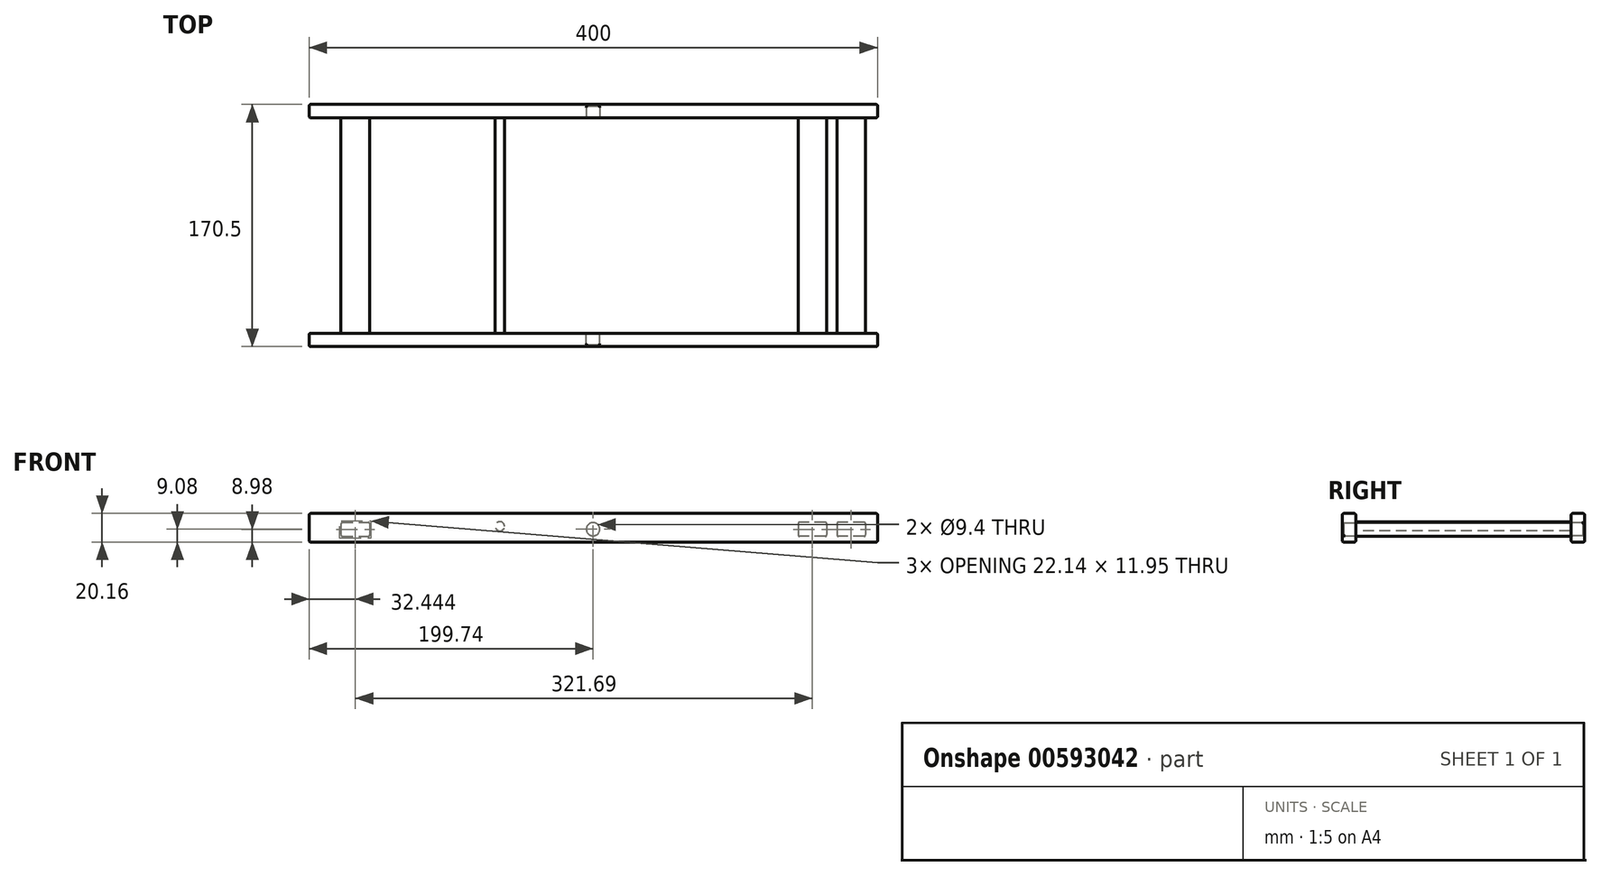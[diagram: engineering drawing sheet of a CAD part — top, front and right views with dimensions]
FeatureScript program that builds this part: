
annotation { "Feature Type Name" : "Feature", "Feature Type Description" : "" }
export const myFeature = defineFeature(function(context is Context, id is Id, definition is map)
    precondition{}
    {
        {
            var Q0;
            Q0=qCreatedBy(makeId("Front.planeOp"),FACE);
            var sketch = newSketch(context, id + "F0", { "sketchPlane" : qUnion([Q0])});
            skLineSegment(sketch, "E0.bottom", {"start": v(200, -10.07) * mm, "end": v(-200, -10.08) * mm});
            skLineSegment(sketch, "E0.top", {"start": v(200, 10.08) * mm, "end": v(-200, 10.07) * mm});
            skLineSegment(sketch, "E0.left", {"start": v(200, -10.07) * mm, "end": v(200, 10.08) * mm});
            skLineSegment(sketch, "E0.right", {"start": v(-200, -10.08) * mm, "end": v(-200, 10.07) * mm});
            skPoint(sketch, "E0.middle", {"position": v(0, 0) * mm});
            skSolve(sketch);
        }
        {
            var Q0;
            Q0=makeQuery(id+"F0.imprint","IMPRINT",FACE,{"disambiguationData":[TD([[makeQuery(id+"F0.imprint","IMPRINT",EDGE,{"derivedFrom":sQuery(id+"F0.wireOp",EDGE,"E0.bottom")}),-1.0]])]});
            extrude(context, id + "F1", {"entities" : qUnion([Q0]), "depth" : 9.4 * mm});
        }
        {
            var Q0;
            Q0=makeQuery(id+"F1.opExtrude","CAP_FACE",FACE,{"disambiguationData":[OSD([sQuery(id+"F0.wireOp",EDGE,"E0.bottom"),sQuery(id+"F0.wireOp",EDGE,"E0.top"),sQuery(id+"F0.wireOp",EDGE,"E0.left"),sQuery(id+"F0.wireOp",EDGE,"E0.right")])],"isStart":false});
            var sketch = newSketch(context, id + "F2", { "sketchPlane" : qUnion([Q0])});
            skLineSegment(sketch, "E1.bottom", {"start": v(-177.62, 3.87) * mm, "end": v(-157.49, 3.87) * mm});
            skLineSegment(sketch, "E1.top", {"start": v(-177.62, -6.08) * mm, "end": v(-157.49, -6.08) * mm});
            skLineSegment(sketch, "E1.left", {"start": v(-177.62, 3.87) * mm, "end": v(-177.62, -6.08) * mm});
            skLineSegment(sketch, "E1.right", {"start": v(-157.49, 3.87) * mm, "end": v(-157.49, -6.07) * mm});
            skLineSegment(sketch, "E2.bottom", {"start": v(191.5, 3.88) * mm, "end": v(171.36, 3.88) * mm});
            skLineSegment(sketch, "E2.top", {"start": v(191.5, -6.07) * mm, "end": v(171.36, -6.07) * mm});
            skLineSegment(sketch, "E2.left", {"start": v(191.5, 3.88) * mm, "end": v(191.5, -6.07) * mm});
            skLineSegment(sketch, "E2.right", {"start": v(171.36, 3.88) * mm, "end": v(171.36, -6.07) * mm});
            skLineSegment(sketch, "E3.bottom", {"start": v(164.2, 3.88) * mm, "end": v(144.06, 3.88) * mm});
            skLineSegment(sketch, "E3.top", {"start": v(164.2, -6.07) * mm, "end": v(144.06, -6.07) * mm});
            skLineSegment(sketch, "E3.left", {"start": v(164.2, 3.88) * mm, "end": v(164.2, -6.07) * mm});
            skLineSegment(sketch, "E3.right", {"start": v(144.06, 3.88) * mm, "end": v(144.06, -6.07) * mm});
            skSolve(sketch);
        }
        {
            var Q0;
            Q0=makeQuery(id+"F2.imprint","IMPRINT",FACE,{"disambiguationData":[TD([[makeQuery(id+"F2.imprint","IMPRINT",EDGE,{"derivedFrom":sQuery(id+"F2.wireOp",EDGE,"E1.bottom")}),-1.0]])]});
            var Q1;
            Q1=makeQuery(id+"F2.imprint","IMPRINT",FACE,{"disambiguationData":[TD([[makeQuery(id+"F2.imprint","IMPRINT",EDGE,{"derivedFrom":sQuery(id+"F2.wireOp",EDGE,"E3.bottom")}),1.0]])]});
            var Q2;
            Q2=makeQuery(id+"F2.imprint","IMPRINT",FACE,{"disambiguationData":[TD([[makeQuery(id+"F2.imprint","IMPRINT",EDGE,{"derivedFrom":sQuery(id+"F2.wireOp",EDGE,"E2.bottom")}),1.0]])]});
            extrude(context, id + "F3", {"entities" : qUnion([Q0, Q1, Q2]), "operationType" : NewBodyOperationType.ADD, "depth" : 151.7 * mm});
        }
        {
            var Q0;
            Q0=makeQuery(id+"F3.opExtrude","CAP_FACE",FACE,{"disambiguationData":[OSD([sQuery(id+"F2.wireOp",EDGE,"E1.bottom"),sQuery(id+"F2.wireOp",EDGE,"E1.top"),sQuery(id+"F2.wireOp",EDGE,"E1.left"),sQuery(id+"F2.wireOp",EDGE,"E1.right")])],"isStart":false});
            var sketch = newSketch(context, id + "F4", { "sketchPlane" : qUnion([Q0])});
            skLineSegment(sketch, "E4.bottom", {"start": v(200, -10.07) * mm, "end": v(-200, -10.08) * mm});
            skLineSegment(sketch, "E4.top", {"start": v(200, 10.08) * mm, "end": v(-200, 10.08) * mm});
            skLineSegment(sketch, "E4.left", {"start": v(200, -10.07) * mm, "end": v(200, 10.08) * mm});
            skLineSegment(sketch, "E4.right", {"start": v(-200, -10.08) * mm, "end": v(-200, 10.08) * mm});
            skPoint(sketch, "E4.middle", {"position": v(0, 0) * mm});
            skSolve(sketch);
        }
        {
            var Q0;
            Q0=qSketchRegion(id+"F4",true);
            extrude(context, id + "F5", {"entities" : qUnion([Q0]), "operationType" : NewBodyOperationType.ADD, "depth" : 9.4 * mm});
        }
        {
            var Q0;
            Q0=makeQuery(id+"F5.opExtrude","CAP_FACE",FACE,{"disambiguationData":[OSD([sQuery(id+"F4.wireOp",EDGE,"E4.bottom"),sQuery(id+"F4.wireOp",EDGE,"E4.top"),sQuery(id+"F4.wireOp",EDGE,"E4.left"),sQuery(id+"F4.wireOp",EDGE,"E4.right")])],"isStart":true});
            var sketch = newSketch(context, id + "F6", { "sketchPlane" : qUnion([Q0])});
            skCircle(sketch, "E5", {"center": v(0.26, -1) * mm, "radius": 4.7 * mm});
            skLineSegment(sketch, "E6", {"start": v(200, 0) * mm, "end": v(-200, 0) * mm, "construction": true});
            skSolve(sketch);
        }
        {
            var Q0;
            Q0=makeQuery(id+"F6.imprint","IMPRINT",FACE,{"disambiguationData":[TD([[makeQuery(id+"F6.imprint","IMPRINT",EDGE,{"derivedFrom":sQuery(id+"F6.wireOp",EDGE,"E5")}),1.0]])]});
            extrude(context, id + "F7", {"entities" : qUnion([Q0]), "operationType" : NewBodyOperationType.REMOVE, "oppositeDirection" : true, "depth" : 8.4 * mm});
        }
        {
            var Q0;
            Q0=makeQuery(id+"F1.opExtrude","CAP_FACE",FACE,{"disambiguationData":[OSD([sQuery(id+"F0.wireOp",EDGE,"E0.bottom"),sQuery(id+"F0.wireOp",EDGE,"E0.top"),sQuery(id+"F0.wireOp",EDGE,"E0.left"),sQuery(id+"F0.wireOp",EDGE,"E0.right")])],"isStart":false});
            var sketch = newSketch(context, id + "F8", { "sketchPlane" : qUnion([Q0])});
            skLineSegment(sketch, "E7", {"start": v(-200, 0) * mm, "end": v(200, 0) * mm, "construction": true});
            skCircle(sketch, "E8", {"center": v(-0.26, -1) * mm, "radius": 4.7 * mm});
            skSolve(sketch);
        }
        {
            var Q0;
            Q0=makeQuery(id+"F8.imprint","IMPRINT",FACE,{"disambiguationData":[TD([[makeQuery(id+"F8.imprint","IMPRINT",EDGE,{"derivedFrom":sQuery(id+"F8.wireOp",EDGE,"E8")}),1.0]])]});
            extrude(context, id + "F9", {"entities" : qUnion([Q0]), "operationType" : NewBodyOperationType.REMOVE, "oppositeDirection" : true, "depth" : 8.4 * mm});
        }
        {
            var Q0;
            Q0=makeQuery(id+"F5.opExtrude","CAP_FACE",FACE,{"disambiguationData":[OSD([sQuery(id+"F4.wireOp",EDGE,"E4.bottom"),sQuery(id+"F4.wireOp",EDGE,"E4.top"),sQuery(id+"F4.wireOp",EDGE,"E4.left"),sQuery(id+"F4.wireOp",EDGE,"E4.right")])],"isStart":true});
            var sketch = newSketch(context, id + "F10", { "sketchPlane" : qUnion([Q0])});
            skCircle(sketch, "E9", {"center": v(65.84, 1.08) * mm, "radius": 3.25 * mm});
            skSolve(sketch);
        }
        {
            var Q0;
            Q0=makeQuery(id+"F10.imprint","IMPRINT",FACE,{"disambiguationData":[TD([[makeQuery(id+"F10.imprint","IMPRINT",EDGE,{"derivedFrom":sQuery(id+"F10.wireOp",EDGE,"E9")}),1.0]])]});
            var Q1;
            Q1=makeQuery(id+"F1.opExtrude","CAP_FACE",FACE,{"disambiguationData":[OSD([sQuery(id+"F0.wireOp",EDGE,"E0.bottom"),sQuery(id+"F0.wireOp",EDGE,"E0.top"),sQuery(id+"F0.wireOp",EDGE,"E0.left"),sQuery(id+"F0.wireOp",EDGE,"E0.right")])],"isStart":false});
            extrude(context, id + "F11", {"entities" : qUnion([Q0]), "operationType" : NewBodyOperationType.ADD, "endBound" : BoundingType.UP_TO_SURFACE, "endBoundEntityFace" : qUnion([Q1]), "depth" : 25 * mm});
        }
        {
            var Q0;
            Q0=makeQuery(id+"F5.opExtrude","CAP_FACE",FACE,{"disambiguationData":[OSD([sQuery(id+"F4.wireOp",EDGE,"E4.bottom"),sQuery(id+"F4.wireOp",EDGE,"E4.top"),sQuery(id+"F4.wireOp",EDGE,"E4.left"),sQuery(id+"F4.wireOp",EDGE,"E4.right")])],"isStart":false});
            var Q1;
            Q1=makeQuery(id+"F3.opExtrude","SWEPT_FACE",FACE,{"disambiguationData":[OSD([sQuery(id+"F2.wireOp",EDGE,"E2.bottom")])]});
            var Q2;
            Q2=makeQuery(id+"F3.opExtrude","SWEPT_FACE",FACE,{"disambiguationData":[OSD([sQuery(id+"F2.wireOp",EDGE,"E3.bottom")])]});
            var Q3;
            Q3=makeQuery(id+"F1.opExtrude","CAP_FACE",FACE,{"disambiguationData":[OSD([sQuery(id+"F0.wireOp",EDGE,"E0.bottom"),sQuery(id+"F0.wireOp",EDGE,"E0.top"),sQuery(id+"F0.wireOp",EDGE,"E0.left"),sQuery(id+"F0.wireOp",EDGE,"E0.right")])],"isStart":false});
            var Q4;
            Q4=makeQuery(id+"F5.opExtrude","SWEPT_FACE",FACE,{"disambiguationData":[OSD([sQuery(id+"F4.wireOp",EDGE,"E4.left")])]});
            var Q5;
            Q5=makeQuery(id+"F5.opExtrude","CAP_EDGE",EDGE,{"disambiguationData":[OSD([sQuery(id+"F4.wireOp",EDGE,"E4.top")])],"isStart":true});
            var Q6;
            Q6=makeQuery(id+"F1.opExtrude","SWEPT_FACE",FACE,{"disambiguationData":[OSD([sQuery(id+"F0.wireOp",EDGE,"E0.top")])]});
            var Q7;
            Q7=makeQuery(id+"F1.opExtrude","SWEPT_FACE",FACE,{"disambiguationData":[OSD([sQuery(id+"F0.wireOp",EDGE,"E0.left")])]});
            var Q8;
            Q8=makeQuery(id+"F3.opExtrude","SWEPT_FACE",FACE,{"disambiguationData":[OSD([sQuery(id+"F2.wireOp",EDGE,"E1.right")])]});
            var Q9;
            Q9=makeQuery(id+"F3.opExtrude","SWEPT_FACE",FACE,{"disambiguationData":[OSD([sQuery(id+"F2.wireOp",EDGE,"E1.bottom")])]});
            var Q10;
            Q10=makeQuery(id+"F5.opExtrude","SWEPT_FACE",FACE,{"disambiguationData":[OSD([sQuery(id+"F4.wireOp",EDGE,"E4.right")])]});
            var Q11;
            Q11=makeQuery(id+"F5.opExtrude","SWEPT_FACE",FACE,{"disambiguationData":[OSD([sQuery(id+"F4.wireOp",EDGE,"E4.bottom")])]});
            var Q12;
            Q12=makeQuery(id+"F3.opExtrude","SWEPT_FACE",FACE,{"disambiguationData":[OSD([sQuery(id+"F2.wireOp",EDGE,"E1.left")])]});
            var Q13;
            Q13=makeQuery(id+"F3.opExtrude","SWEPT_FACE",FACE,{"disambiguationData":[OSD([sQuery(id+"F2.wireOp",EDGE,"E1.top")])]});
            var Q14;
            Q14=makeQuery(id+"F5.opExtrude","CAP_FACE",FACE,{"disambiguationData":[OSD([sQuery(id+"F4.wireOp",EDGE,"E4.bottom"),sQuery(id+"F4.wireOp",EDGE,"E4.top"),sQuery(id+"F4.wireOp",EDGE,"E4.left"),sQuery(id+"F4.wireOp",EDGE,"E4.right")])],"isStart":true});
            var Q15;
            Q15=makeQuery(id+"F1.opExtrude","SWEPT_FACE",FACE,{"disambiguationData":[OSD([sQuery(id+"F0.wireOp",EDGE,"E0.right")])]});
            var Q16;
            Q16=makeQuery(id+"F1.opExtrude","CAP_FACE",FACE,{"disambiguationData":[OSD([sQuery(id+"F0.wireOp",EDGE,"E0.bottom"),sQuery(id+"F0.wireOp",EDGE,"E0.top"),sQuery(id+"F0.wireOp",EDGE,"E0.left"),sQuery(id+"F0.wireOp",EDGE,"E0.right")])],"isStart":true});
            var Q17;
            Q17=makeQuery(id+"F3.opExtrude","SWEPT_FACE",FACE,{"disambiguationData":[OSD([sQuery(id+"F2.wireOp",EDGE,"E2.top")])]});
            var Q18;
            Q18=makeQuery(id+"F3.opExtrude","SWEPT_FACE",FACE,{"disambiguationData":[OSD([sQuery(id+"F2.wireOp",EDGE,"E3.top")])]});
            var Q19;
            Q19=makeQuery(id+"F3.opExtrude","SWEPT_FACE",FACE,{"disambiguationData":[OSD([sQuery(id+"F2.wireOp",EDGE,"E3.left")])]});
            var Q20;
            Q20=makeQuery(id+"F7.boolean.opBoolean","COPY",FACE,{"derivedFrom":makeQuery(id+"F7.opExtrude","CAP_FACE",FACE,{"disambiguationData":[OSD([sQuery(id+"F6.wireOp",EDGE,"E5")])],"isStart":false})});
            var Q21;
            Q21=makeQuery(id+"F9.boolean.opBoolean","COPY",EDGE,{"derivedFrom":makeQuery(id+"F9.opExtrude","CAP_EDGE",EDGE,{"disambiguationData":[OSD([sQuery(id+"F8.wireOp",EDGE,"E8")])],"isStart":false})});
            fillet(context, id + "F12", {"entities" : qUnion([Q0, Q1, Q2, Q3, Q4, Q5, Q6, Q7, Q8, Q9, Q10, Q11, Q12, Q13, Q14, Q15, Q16, Q17, Q18, Q19, Q20, Q21]), "radius" : 1 * mm, "tangentPropagation" : true, "allowEdgeOverflow" : false});
        }
    });
